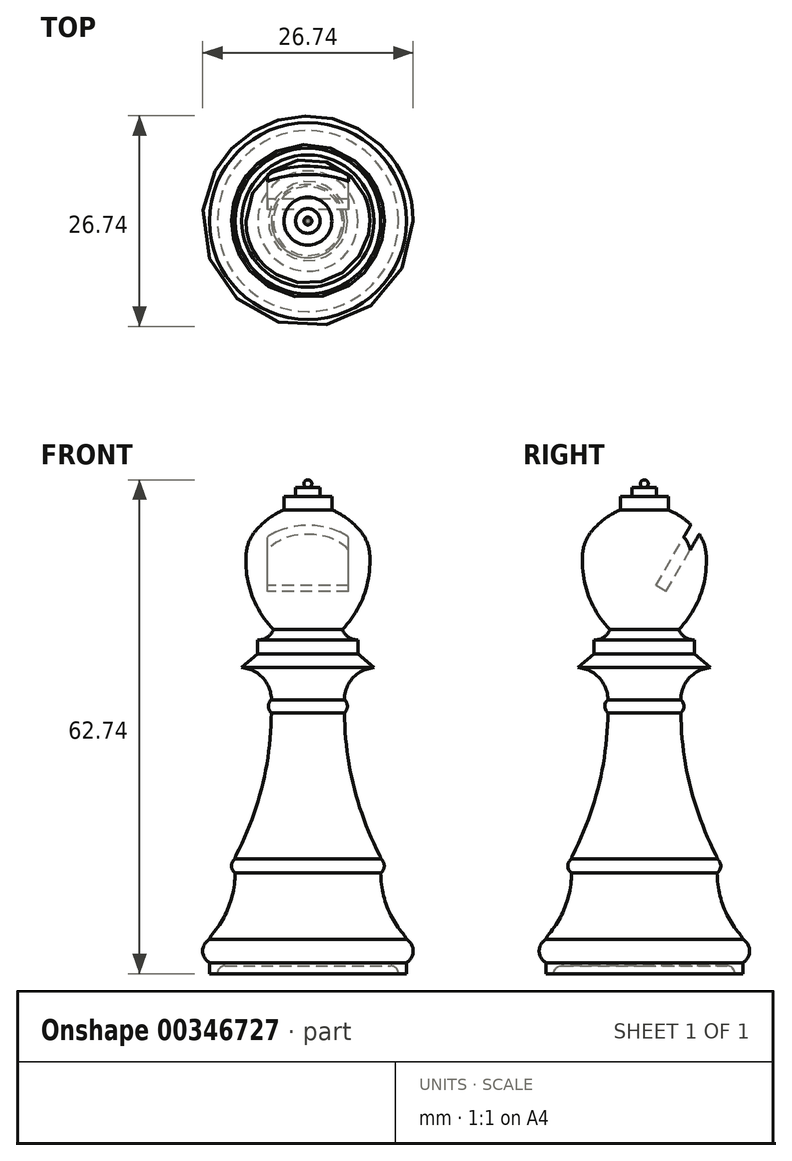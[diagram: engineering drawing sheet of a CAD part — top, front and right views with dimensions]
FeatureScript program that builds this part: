
annotation { "Feature Type Name" : "Feature", "Feature Type Description" : "" }
export const myFeature = defineFeature(function(context is Context, id is Id, definition is map)
    precondition{}
    {
        {
            var Q0;
            Q0=qCreatedBy(makeId("Front.planeOp"),FACE);
            var sketch = newSketch(context, id + "F0", { "sketchPlane" : qUnion([Q0])});
            skLineSegment(sketch, "E0", {"start": v(-100.9, 26.37) * mm, "end": v(-100.9, 27.76) * mm});
            skArc(sketch, "E1", {"start": v(-100.9, 27.76) * mm, "mid": v(-100.04, 29.24) * mm, "end": v(-100.9, 30.72) * mm});
            skLineSegment(sketch, "E2", {"start": v(-100.9, 30.72) * mm, "end": v(-100.9, 32.11) * mm});
            skLineSegment(sketch, "E3", {"start": v(-104.16, 39.17) * mm, "end": v(-104.16, 32.11) * mm});
            skLineSegment(sketch, "E4", {"start": v(-104.16, 32.11) * mm, "end": v(-100.9, 32.11) * mm});
            skArc(sketch, "E5", {"start": v(-104.16, 39.17) * mm, "mid": v(-103.7, 40.06) * mm, "end": v(-104.16, 40.96) * mm});
            skLineSegment(sketch, "E6", {"start": v(-104.16, 40.96) * mm, "end": v(-104.16, 42.27) * mm});
            skLineSegment(sketch, "E7", {"start": v(-108.77, 59.52) * mm, "end": v(-108.77, 42.27) * mm});
            skLineSegment(sketch, "E8", {"start": v(-108.77, 42.27) * mm, "end": v(-104.16, 42.27) * mm});
            skArc(sketch, "E9", {"start": v(-108.77, 59.52) * mm, "mid": v(-108.39, 60.34) * mm, "end": v(-108.77, 61.17) * mm});
            skLineSegment(sketch, "E10", {"start": v(-108.77, 61.17) * mm, "end": v(-108.77, 65.24) * mm});
            skLineSegment(sketch, "E11", {"start": v(-108.77, 65.24) * mm, "end": v(-105, 65.24) * mm});
            skLineSegment(sketch, "E12", {"start": v(-105, 65.24) * mm, "end": v(-107.04, 67) * mm});
            skLineSegment(sketch, "E13", {"start": v(-107.04, 67) * mm, "end": v(-107.04, 68.75) * mm});
            skLineSegment(sketch, "E14", {"start": v(-107.04, 68.75) * mm, "end": v(-109.04, 68.75) * mm});
            skLineSegment(sketch, "E15", {"start": v(-109.04, 68.75) * mm, "end": v(-109.04, 70.1) * mm});
            skLineSegment(sketch, "E16", {"start": v(-110.36, 85.28) * mm, "end": v(-110.36, 86.98) * mm});
            skLineSegment(sketch, "E17", {"start": v(-110.36, 86.98) * mm, "end": v(-111.85, 86.98) * mm});
            skLineSegment(sketch, "E18", {"start": v(-111.85, 86.98) * mm, "end": v(-111.85, 88.16) * mm});
            skLineSegment(sketch, "E19", {"start": v(-113.4, 88.16) * mm, "end": v(-113.4, 26.37) * mm});
            skLineSegment(sketch, "E20", {"start": v(-113.4, 26.37) * mm, "end": v(-100.9, 26.37) * mm});
            skArc(sketch, "E21", {"start": v(-105.78, 81.21) * mm, "mid": v(-107.74, 83.62) * mm, "end": v(-110.36, 85.28) * mm});
            skArc(sketch, "E22", {"start": v(-109.04, 70.1) * mm, "mid": v(-106.03, 75.25) * mm, "end": v(-105.78, 81.21) * mm});
            skPoint(sketch, "E23", {"position": v(-113.4, 88.11) * mm});
            skLineSegment(sketch, "E24", {"start": v(-113.4, 88.16) * mm, "end": v(-113.4, 89.11) * mm});
            skLineSegment(sketch, "E25", {"start": v(-111.85, 88.16) * mm, "end": v(-113.2, 88.16) * mm});
            skArc(sketch, "E26", {"start": v(-113.4, 89.11) * mm, "mid": v(-112.92, 88.72) * mm, "end": v(-113.2, 88.16) * mm});
            skSolve(sketch);
        }
        {
            var Q0;
            Q0=makeQuery(id+"F0.imprint","IMPRINT",FACE,{"disambiguationData":[TD([[makeQuery(id+"F0.imprint","IMPRINT",EDGE,{"derivedFrom":sQuery(id+"F0.wireOp",EDGE,"E0")}),1.0]])]});
            var Q1;
            Q1=sQuery(id+"F0.wireOp",EDGE,"E19");
            revolve(context, id + "F1", {"entities" : qUnion([Q0]), "axis" : qUnion([Q1]), "revolveType" : RevolveType.FULL});
        }
        {
            var Q0;
            Q0=makeQuery(id+"F1.opRevolve","SWEPT_EDGE",EDGE,{"disambiguationData":[OSD([sQuery(id+"F0.wireOp",EDGE,"E2"),sQuery(id+"F0.wireOp",EDGE,"E4")])]});
            fillet(context, id + "F2", {"entities" : qUnion([Q0]), "radius" : 2 * mm, "tangentPropagation" : true, "allowEdgeOverflow" : false});
        }
        {
            var Q0;
            Q0=makeQuery(id+"F1.opRevolve","SWEPT_EDGE",EDGE,{"disambiguationData":[OSD([sQuery(id+"F0.wireOp",EDGE,"E3"),sQuery(id+"F0.wireOp",EDGE,"E4")])]});
            fillet(context, id + "F3", {"entities" : qUnion([Q0]), "radius" : 12 * mm, "tangentPropagation" : true, "allowEdgeOverflow" : false});
        }
        {
            var Q0;
            Q0=makeQuery(id+"F1.opRevolve","SWEPT_EDGE",EDGE,{"disambiguationData":[OSD([sQuery(id+"F0.wireOp",EDGE,"E6"),sQuery(id+"F0.wireOp",EDGE,"E8")])]});
            fillet(context, id + "F4", {"entities" : qUnion([Q0]), "radius" : 1.5 * mm, "tangentPropagation" : true, "allowEdgeOverflow" : false});
        }
        {
            var Q0;
            Q0=makeQuery(id+"F1.opRevolve","SWEPT_EDGE",EDGE,{"disambiguationData":[OSD([sQuery(id+"F0.wireOp",EDGE,"E7"),sQuery(id+"F0.wireOp",EDGE,"E8")])]});
            fillet(context, id + "F5", {"entities" : qUnion([Q0]), "radius" : 40 * mm, "tangentPropagation" : true, "allowEdgeOverflow" : false});
        }
        {
            var Q0;
            Q0=makeQuery(id+"F1.opRevolve","SWEPT_EDGE",EDGE,{"disambiguationData":[OSD([sQuery(id+"F0.wireOp",EDGE,"E10"),sQuery(id+"F0.wireOp",EDGE,"E11")])]});
            fillet(context, id + "F6", {"entities" : qUnion([Q0]), "radius" : 4.08 * mm, "tangentPropagation" : true, "allowEdgeOverflow" : false});
        }
        {
            var Q0;
            Q0=makeQuery(id+"F1.opRevolve","SWEPT_EDGE",EDGE,{"disambiguationData":[OSD([sQuery(id+"F0.wireOp",EDGE,"E14"),sQuery(id+"F0.wireOp",EDGE,"E15")])]});
            fillet(context, id + "F7", {"entities" : qUnion([Q0]), "radius" : 2.14 * mm, "tangentPropagation" : true, "allowEdgeOverflow" : false});
        }
        {
            var Q0;
            Q0=makeQuery(id+"F1.opRevolve","SWEPT_FACE",FACE,{"disambiguationData":[OSD([sQuery(id+"F0.wireOp",EDGE,"E25")])]});
            cPlane(context, id + "F8", {"entities" : qUnion([Q0]), "cplaneType" : CPlaneType.OFFSET, "offset" : 0.1 * mm, "oppositeDirection" : true, "width" : 150 * mm, "height" : 150 * mm});
        }
        {
            var Q0;
            Q0=makeQuery(id+"F1.opRevolve","SWEPT_EDGE",EDGE,{"disambiguationData":[OSD([sQuery(id+"F0.wireOp",EDGE,"E21"),sQuery(id+"F0.wireOp",EDGE,"E22")])]});
            fillet(context, id + "F9", {"entities" : qUnion([Q0]), "radius" : 5 * mm, "tangentPropagation" : true, "allowEdgeOverflow" : false});
        }
        {
            var Q0;
            Q0=qCreatedBy(id+"F8.planeOp",FACE);
            var sketch = newSketch(context, id + "F10", { "sketchPlane" : qUnion([Q0])});
            skLineSegment(sketch, "E27", {"start": v(-110.39, 0) * mm, "end": v(-116.55, 0) * mm});
            skSolve(sketch);
        }
        {
            var Q0;
            Q0=qCreatedBy(id+"F8.planeOp",FACE);
            var Q1;
            Q1=sQuery(id+"F10.wireOp",EDGE,"E27");
            cPlane(context, id + "F11", {"entities" : qUnion([Q0, Q1]), "cplaneType" : CPlaneType.LINE_ANGLE, "offset" : 1 * mm, "angle" : 30 * degree, "width" : 150 * mm, "height" : 150 * mm});
        }
        {
            var Q0;
            Q0=qCreatedBy(id+"F11.planeOp",FACE);
            var sketch = newSketch(context, id + "F12", { "sketchPlane" : qUnion([Q0])});
            skLineSegment(sketch, "E28.top", {"start": v(-108.26, 35.06) * mm, "end": v(-118.56, 35.06) * mm});
            skLineSegment(sketch, "E29.top", {"start": v(-108.26, 36.57) * mm, "end": v(-118.56, 36.57) * mm});
            skLineSegment(sketch, "E29.left", {"start": v(-108.26, 35.06) * mm, "end": v(-108.26, 36.57) * mm});
            skLineSegment(sketch, "E29.right", {"start": v(-118.56, 35.06) * mm, "end": v(-118.56, 36.57) * mm});
            skSolve(sketch);
        }
        {
            var Q0;
            Q0=makeQuery(id+"F12.imprint","IMPRINT",FACE,{"disambiguationData":[TD([[makeQuery(id+"F12.imprint","IMPRINT",EDGE,{"derivedFrom":sQuery(id+"F12.wireOp",EDGE,"E28.top")}),-1.0]])]});
            extrude(context, id + "F13", {"entities" : qUnion([Q0]), "operationType" : NewBodyOperationType.REMOVE, "depth" : 10 * mm});
        }
        {
            var Q0;
            Q0=makeQuery(id+"F1.opRevolve","SWEPT_FACE",FACE,{"disambiguationData":[OSD([sQuery(id+"F0.wireOp",EDGE,"E20")])]});
            var sketch = newSketch(context, id + "F14", { "sketchPlane" : qUnion([Q0])});
            skCircle(sketch, "E30", {"center": v(-113.4, 0) * mm, "radius": 11.5 * mm});
            skSolve(sketch);
        }
        {
            var Q0;
            Q0 = qSketchRegion(id + "F14", true);
            extrude(context, id + "F15", {"entities" : qUnion([Q0]), "operationType" : NewBodyOperationType.REMOVE, "oppositeDirection" : true, "depth" : 1 * mm});
        }
        {
            var Q0;
            Q0=makeQuery(id+"F15.boolean.opBoolean","COPY",EDGE,{"derivedFrom":makeQuery(id+"F15.opExtrude","CAP_EDGE",EDGE,{"disambiguationData":[OSD([sQuery(id+"F14.wireOp",EDGE,"E30")])],"isStart":false})});
            fillet(context, id + "F16", {"entities" : qUnion([Q0]), "radius" : 1 * mm, "tangentPropagation" : true, "allowEdgeOverflow" : false});
        }
    });
